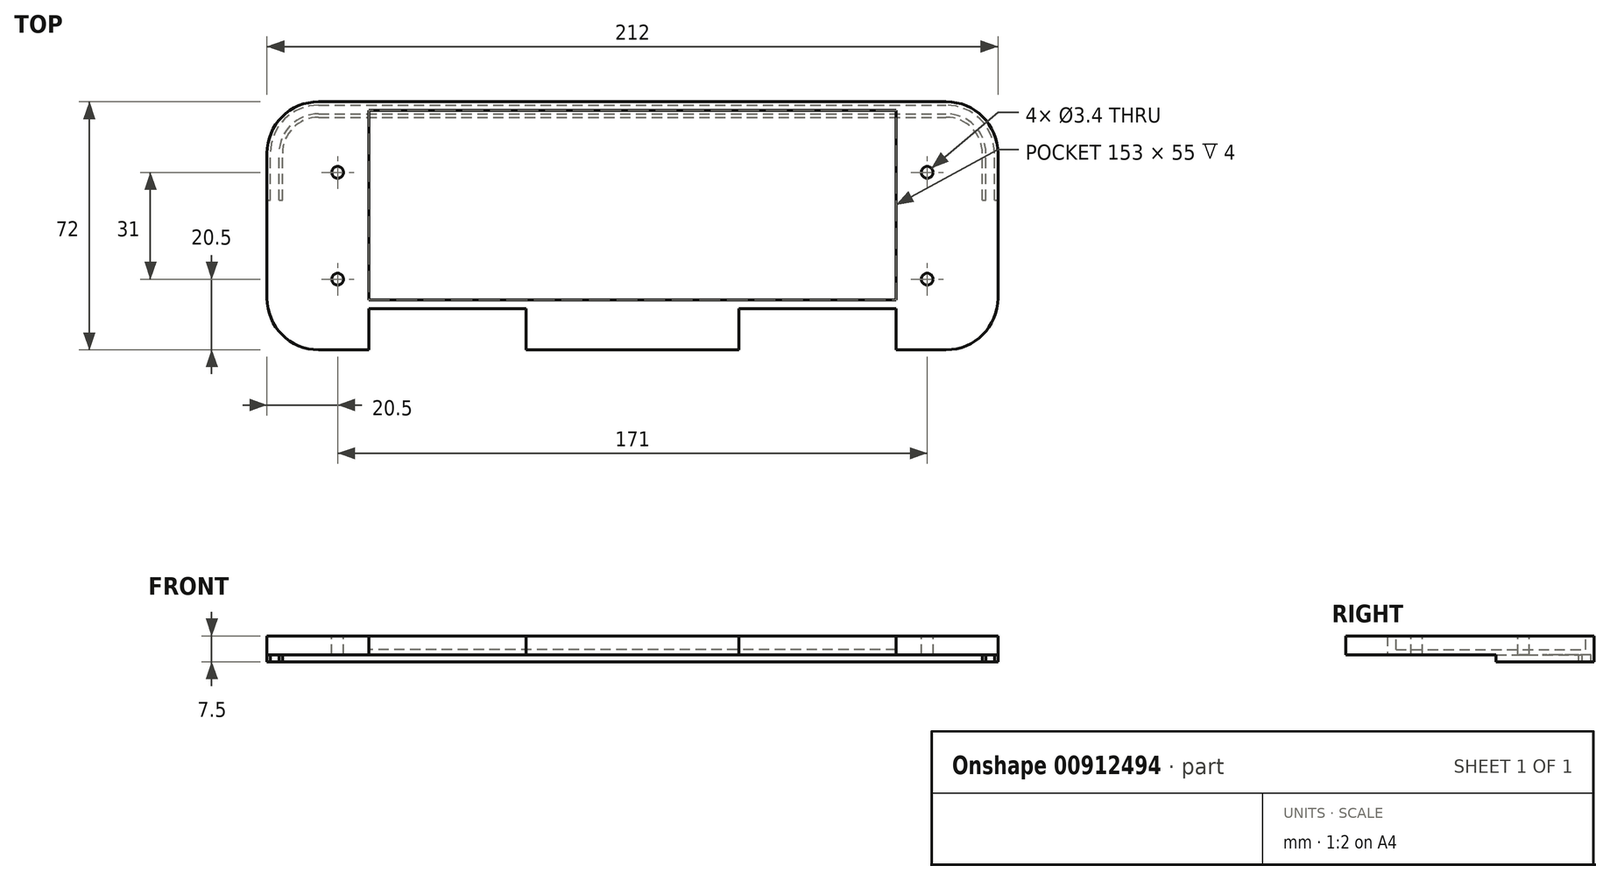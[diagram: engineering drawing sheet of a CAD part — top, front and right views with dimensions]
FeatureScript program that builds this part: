
annotation { "Feature Type Name" : "Feature", "Feature Type Description" : "" }
export const myFeature = defineFeature(function(context is Context, id is Id, definition is map)
    precondition{}
    {
        {
            var Q0;
            Q0=qCreatedBy(makeId("Top.planeOp"),FACE);
            var sketch = newSketch(context, id + "F0", { "sketchPlane" : qUnion([Q0])});
            skLineSegment(sketch, "E0.bottom", {"start": v(-106, 36) * mm, "end": v(106, 36) * mm});
            skLineSegment(sketch, "E0.top", {"start": v(-106, -36) * mm, "end": v(106, -36) * mm});
            skLineSegment(sketch, "E0.left", {"start": v(-106, 36) * mm, "end": v(-106, -36) * mm});
            skLineSegment(sketch, "E0.right", {"start": v(106, 36) * mm, "end": v(106, -36) * mm});
            skPoint(sketch, "E0.middle", {"position": v(0, 0) * mm});
            skSolve(sketch);
        }
        {
            var Q0;
            Q0 = qSketchRegion(id + "F0", true);
            extrude(context, id + "F1", {"entities" : qUnion([Q0]), "depth" : 5.5 * mm, "offsetDistance" : 25 * mm});
        }
        {
            var Q0;
            Q0=makeQuery(id+"F1.opExtrude","SWEPT_EDGE",EDGE,{"disambiguationData":[OSD([sQuery(id+"F0.wireOp",EDGE,"E0.top"),sQuery(id+"F0.wireOp",EDGE,"E0.left")])]});
            var Q1;
            Q1=makeQuery(id+"F1.opExtrude","SWEPT_EDGE",EDGE,{"disambiguationData":[OSD([sQuery(id+"F0.wireOp",EDGE,"E0.top"),sQuery(id+"F0.wireOp",EDGE,"E0.right")])]});
            fillet(context, id + "F2", {"entities" : qUnion([Q0, Q1]), "radius" : 15 * mm, "tangentPropagation" : true, "allowEdgeOverflow" : false});
        }
        {
            var Q0;
            Q0=makeQuery(id+"F1.opExtrude","SWEPT_FACE",FACE,{"disambiguationData":[OSD([sQuery(id+"F0.wireOp",EDGE,"E0.top")])]});
            var sketch = newSketch(context, id + "F3", { "sketchPlane" : qUnion([Q0])});
            skLineSegment(sketch, "E1.bottom", {"start": v(-76.5, 5.5) * mm, "end": v(-30.88, 5.5) * mm});
            skLineSegment(sketch, "E1.top", {"start": v(-76.5, 0) * mm, "end": v(-30.88, 0) * mm});
            skLineSegment(sketch, "E1.left", {"start": v(-76.5, 5.5) * mm, "end": v(-76.5, 0) * mm});
            skLineSegment(sketch, "E1.right", {"start": v(-30.88, 5.5) * mm, "end": v(-30.88, 0) * mm});
            skLineSegment(sketch, "E2.bottom", {"start": v(30.88, 5.5) * mm, "end": v(76.5, 5.5) * mm});
            skLineSegment(sketch, "E2.top", {"start": v(30.88, 0) * mm, "end": v(76.5, 0) * mm});
            skLineSegment(sketch, "E2.left", {"start": v(30.88, 5.5) * mm, "end": v(30.88, 0) * mm});
            skLineSegment(sketch, "E2.right", {"start": v(76.5, 5.5) * mm, "end": v(76.5, 0) * mm});
            skSolve(sketch);
        }
        {
            var Q0;
            Q0 = qSketchRegion(id + "F3", true);
            extrude(context, id + "F4", {"entities" : qUnion([Q0]), "operationType" : NewBodyOperationType.REMOVE, "oppositeDirection" : true, "depth" : 12 * mm, "offsetDistance" : 25 * mm});
        }
        {
            var Q0;
            Q0=makeQuery(id+"F1.opExtrude","CAP_FACE",FACE,{"disambiguationData":[OSD([sQuery(id+"F0.wireOp",EDGE,"E0.bottom"),sQuery(id+"F0.wireOp",EDGE,"E0.top"),sQuery(id+"F0.wireOp",EDGE,"E0.left"),sQuery(id+"F0.wireOp",EDGE,"E0.right")])],"isStart":true});
            var sketch = newSketch(context, id + "F5", { "sketchPlane" : qUnion([Q0])});
            skLineSegment(sketch, "E3.bottom", {"start": v(-106, -7.5) * mm, "end": v(-105, -7.5) * mm});
            skLineSegment(sketch, "E3.top", {"start": v(-106, -36) * mm, "end": v(106, -36) * mm});
            skLineSegment(sketch, "E3.left", {"start": v(-106, -7.5) * mm, "end": v(-106, -36) * mm});
            skLineSegment(sketch, "E3.right", {"start": v(106, -7.5) * mm, "end": v(106, -36) * mm});
            skLineSegment(sketch, "E4.top", {"start": v(-101.5, -31.5) * mm, "end": v(101.5, -31.5) * mm});
            skLineSegment(sketch, "E4.left", {"start": v(-101.5, -7.5) * mm, "end": v(-101.5, -31.5) * mm});
            skLineSegment(sketch, "E4.right", {"start": v(101.5, -7.5) * mm, "end": v(101.5, -31.5) * mm});
            skLineSegment(sketch, "E5.trimOffspring", {"start": v(101.5, -7.5) * mm, "end": v(102.5, -7.5) * mm});
            skLineSegment(sketch, "E6.bottom", {"start": v(-102.5, -7.5) * mm, "end": v(-101.5, -7.5) * mm});
            skLineSegment(sketch, "E6.top", {"start": v(-105, -35) * mm, "end": v(105, -35) * mm});
            skLineSegment(sketch, "E6.left", {"start": v(-105, -7.5) * mm, "end": v(-105, -35) * mm});
            skLineSegment(sketch, "E6.right", {"start": v(105, -7.5) * mm, "end": v(105, -35) * mm});
            skLineSegment(sketch, "E7.top", {"start": v(-102.5, -32.5) * mm, "end": v(102.5, -32.5) * mm});
            skLineSegment(sketch, "E7.left", {"start": v(-102.5, -7.5) * mm, "end": v(-102.5, -32.5) * mm});
            skLineSegment(sketch, "E7.right", {"start": v(102.5, -7.5) * mm, "end": v(102.5, -32.5) * mm});
            skLineSegment(sketch, "E8.trimOffspring", {"start": v(105, -7.5) * mm, "end": v(106, -7.5) * mm});
            skSolve(sketch);
        }
        {
            var Q0;
            Q0 = qSketchRegion(id + "F5", true);
            extrude(context, id + "F6", {"entities" : qUnion([Q0]), "operationType" : NewBodyOperationType.ADD, "depth" : 2 * mm, "offsetDistance" : 25 * mm});
        }
        {
            var Q0;
            Q0=makeQuery(id+"F6.opExtrude","SWEPT_EDGE",EDGE,{"disambiguationData":[OSD([sQuery(id+"F5.wireOp",EDGE,"E4.top"),sQuery(id+"F5.wireOp",EDGE,"E4.right")])]});
            var Q1;
            Q1=makeQuery(id+"F6.opExtrude","SWEPT_EDGE",EDGE,{"disambiguationData":[OSD([sQuery(id+"F5.wireOp",EDGE,"E4.top"),sQuery(id+"F5.wireOp",EDGE,"E4.left")])]});
            fillet(context, id + "F7", {"entities" : qUnion([Q0, Q1]), "radius" : 10.5 * mm, "tangentPropagation" : true, "allowEdgeOverflow" : false});
        }
        {
            var Q0;
            Q0=makeQuery(id+"F6.opExtrude","SWEPT_EDGE",EDGE,{"disambiguationData":[OSD([sQuery(id+"F5.wireOp",EDGE,"E7.top"),sQuery(id+"F5.wireOp",EDGE,"E7.right")])]});
            var Q1;
            Q1=makeQuery(id+"F6.opExtrude","SWEPT_EDGE",EDGE,{"disambiguationData":[OSD([sQuery(id+"F5.wireOp",EDGE,"E7.top"),sQuery(id+"F5.wireOp",EDGE,"E7.left")])]});
            fillet(context, id + "F8", {"entities" : qUnion([Q0, Q1]), "radius" : 11.5 * mm, "tangentPropagation" : true, "allowEdgeOverflow" : false});
        }
        {
            var Q0;
            Q0=makeQuery(id+"F6.opExtrude","SWEPT_EDGE",EDGE,{"disambiguationData":[OSD([sQuery(id+"F5.wireOp",EDGE,"E6.top"),sQuery(id+"F5.wireOp",EDGE,"E6.right")])]});
            var Q1;
            Q1=makeQuery(id+"F6.opExtrude","SWEPT_EDGE",EDGE,{"disambiguationData":[OSD([sQuery(id+"F5.wireOp",EDGE,"E6.top"),sQuery(id+"F5.wireOp",EDGE,"E6.left")])]});
            fillet(context, id + "F9", {"entities" : qUnion([Q0, Q1]), "radius" : 14 * mm, "tangentPropagation" : true, "allowEdgeOverflow" : false});
        }
        {
            var Q0;
            Q0=makeQuery(id+"F6.boolean.opBoolean","MERGE",EDGE,{"derivedFrom":[makeQuery(id+"F1.opExtrude","SWEPT_EDGE",EDGE,{"disambiguationData":[OSD([sQuery(id+"F0.wireOp",EDGE,"E0.bottom"),sQuery(id+"F0.wireOp",EDGE,"E0.right")])]}),makeQuery(id+"F6.opExtrude","SWEPT_EDGE",EDGE,{"disambiguationData":[OSD([sQuery(id+"F5.wireOp",EDGE,"E3.top"),sQuery(id+"F5.wireOp",EDGE,"E3.right")])]})]});
            var Q1;
            Q1=makeQuery(id+"F6.boolean.opBoolean","MERGE",EDGE,{"derivedFrom":[makeQuery(id+"F1.opExtrude","SWEPT_EDGE",EDGE,{"disambiguationData":[OSD([sQuery(id+"F0.wireOp",EDGE,"E0.bottom"),sQuery(id+"F0.wireOp",EDGE,"E0.left")])]}),makeQuery(id+"F6.opExtrude","SWEPT_EDGE",EDGE,{"disambiguationData":[OSD([sQuery(id+"F5.wireOp",EDGE,"E3.top"),sQuery(id+"F5.wireOp",EDGE,"E3.left")])]})]});
            fillet(context, id + "F10", {"entities" : qUnion([Q0, Q1]), "radius" : 15 * mm, "tangentPropagation" : true, "allowEdgeOverflow" : false});
        }
        {
            var Q0;
            Q0=makeQuery(id+"F1.opExtrude","CAP_FACE",FACE,{"disambiguationData":[OSD([sQuery(id+"F0.wireOp",EDGE,"E0.bottom"),sQuery(id+"F0.wireOp",EDGE,"E0.top"),sQuery(id+"F0.wireOp",EDGE,"E0.left"),sQuery(id+"F0.wireOp",EDGE,"E0.right")])],"isStart":false});
            var sketch = newSketch(context, id + "F11", { "sketchPlane" : qUnion([Q0])});
            skLineSegment(sketch, "E9.bottom", {"start": v(76.5, 33.5) * mm, "end": v(-76.5, 33.5) * mm});
            skLineSegment(sketch, "E9.top", {"start": v(76.5, -21.5) * mm, "end": v(-76.5, -21.5) * mm});
            skLineSegment(sketch, "E9.left", {"start": v(76.5, -21.5) * mm, "end": v(76.5, 33.5) * mm});
            skLineSegment(sketch, "E9.right", {"start": v(-76.5, -21.5) * mm, "end": v(-76.5, 33.5) * mm});
            skPoint(sketch, "E9.middle", {"position": v(0, 0) * mm});
            skSolve(sketch);
        }
        {
            var Q0;
            Q0 = qSketchRegion(id + "F11", true);
            extrude(context, id + "F12", {"entities" : qUnion([Q0]), "operationType" : NewBodyOperationType.REMOVE, "oppositeDirection" : true, "depth" : 4 * mm, "offsetDistance" : 25 * mm});
        }
        {
            var Q0;
            Q0=makeQuery(id+"F1.opExtrude","CAP_FACE",FACE,{"disambiguationData":[OSD([sQuery(id+"F0.wireOp",EDGE,"E0.bottom"),sQuery(id+"F0.wireOp",EDGE,"E0.top"),sQuery(id+"F0.wireOp",EDGE,"E0.left"),sQuery(id+"F0.wireOp",EDGE,"E0.right")])],"isStart":false});
            var sketch = newSketch(context, id + "F13", { "sketchPlane" : qUnion([Q0])});
            skPoint(sketch, "E10", {"position": v(85.5, 15.5) * mm});
            skPoint(sketch, "E11", {"position": v(85.5, -15.5) * mm});
            skPoint(sketch, "E12", {"position": v(-85.5, 15.5) * mm});
            skPoint(sketch, "E13", {"position": v(-85.5, -15.5) * mm});
            skSolve(sketch);
        }
        {
            var Q0;
            Q0=sQuery(id+"F13.wireOp",VERTEX,"E12");
            var Q1;
            Q1=sQuery(id+"F13.wireOp",VERTEX,"5491ae01-6f72-4d20-b0d5-79ec1aa562b5");
            var Q2;
            Q2=sQuery(id+"F13.wireOp",VERTEX,"E10");
            var Q3;
            Q3=sQuery(id+"F13.wireOp",VERTEX,"E11");
            var Q4;
            Q4=sQuery(id+"F13.wireOp",VERTEX,"E13");
            var Q5;
            Q5=makeQuery(id+"F1.opExtrude","SWEPT_BODY",BODY,{"disambiguationData":[OSD([sQuery(id+"F0.wireOp",EDGE,"E0.bottom"),sQuery(id+"F0.wireOp",EDGE,"E0.top"),sQuery(id+"F0.wireOp",EDGE,"E0.left"),sQuery(id+"F0.wireOp",EDGE,"E0.right")])]});
            hole(context, id + "F14", {"style" : HoleStyle.SIMPLE, "endStyle" : HoleEndStyle.THROUGH, "standardTappedOrClearance" : lookupTablePath({ "fit" : "Normal", "standard" : "ISO", "size" : "M3", "type" : "Clearance" }), "standardBlindInLast" : lookupTablePath({ "fit" : "Normal", "standard" : "ISO", "size" : "M3", "type" : "Clearance" }), "holeDiameter" : 3.4 * mm, "majorDiameter" : 5 * mm, "isTappedThrough" : true, "tappedDepth" : 12 * mm, "tapClearance" : 3, "locations" : qUnion([Q0, Q1, Q2, Q3, Q4]), "scope" : qUnion([Q5])});
        }
    });
